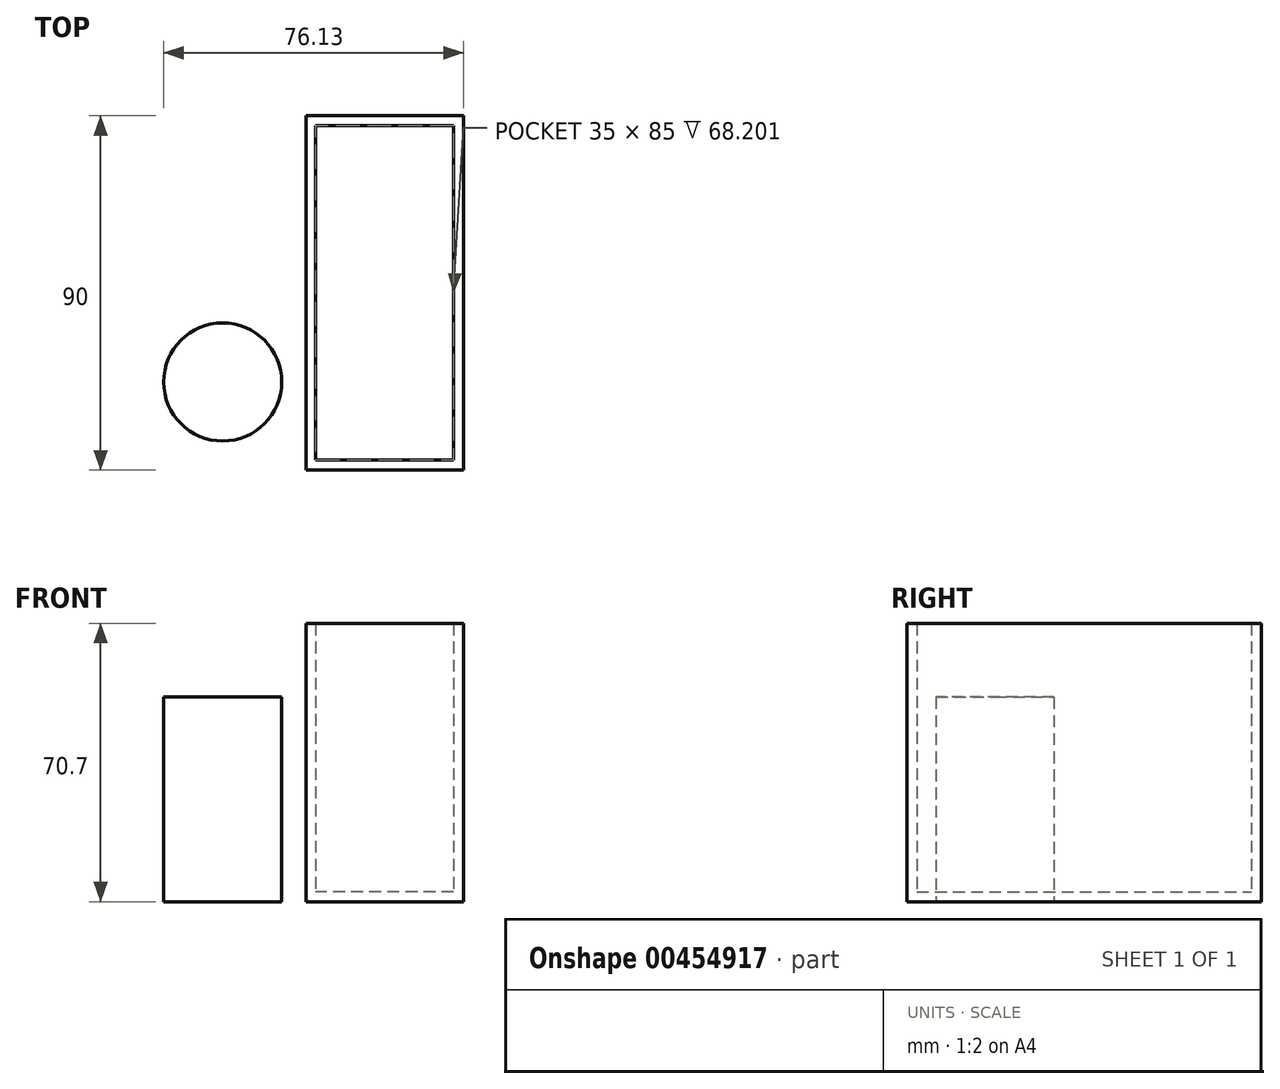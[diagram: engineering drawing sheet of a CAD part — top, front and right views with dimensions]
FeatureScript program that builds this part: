
annotation { "Feature Type Name" : "Feature", "Feature Type Description" : "" }
export const myFeature = defineFeature(function(context is Context, id is Id, definition is map)
    precondition{}
    {
        {
            var Q0;
            Q0=qCreatedBy(makeId("Top.planeOp"),FACE);
            var sketch = newSketch(context, id + "F0", { "sketchPlane" : qUnion([Q0])});
            skCircle(sketch, "E0", {"center": v(0, 0) * mm, "radius": 15 * mm});
            skSolve(sketch);
        }
        {
            var Q0;
            Q0 = qSketchRegion(id + "F0", true);
            var Q1;
            Q1=makeQuery(id+"F0.imprint","IMPRINT",FACE,{"disambiguationData":[TD([[makeQuery(id+"F0.imprint","IMPRINT",EDGE,{"derivedFrom":sQuery(id+"F0.wireOp",EDGE,"E0")}),1.0]])]});
            extrude(context, id + "F1", {"entities" : qUnion([Q0, Q1]), "depth" : 52 * mm});
        }
        {
            var Q0;
            Q0=qCreatedBy(makeId("Top.planeOp"),FACE);
            var sketch = newSketch(context, id + "F2", { "sketchPlane" : qUnion([Q0])});
            skLineSegment(sketch, "E1.bottom", {"start": v(61.13, -22.35) * mm, "end": v(21.13, -22.35) * mm});
            skLineSegment(sketch, "E1.top", {"start": v(61.13, 67.65) * mm, "end": v(21.13, 67.65) * mm});
            skLineSegment(sketch, "E1.left", {"start": v(61.13, -22.35) * mm, "end": v(61.13, 67.65) * mm});
            skLineSegment(sketch, "E1.right", {"start": v(21.13, -22.35) * mm, "end": v(21.13, 67.65) * mm});
            skPoint(sketch, "E1.middle", {"position": v(41.13, 22.65) * mm});
            skSolve(sketch);
        }
        {
            var Q0;
            Q0=makeQuery(id+"F2.imprint","IMPRINT",FACE,{"disambiguationData":[TD([[makeQuery(id+"F2.imprint","IMPRINT",EDGE,{"derivedFrom":sQuery(id+"F2.wireOp",EDGE,"E1.bottom")}),-1.0]])]});
            extrude(context, id + "F3", {"entities" : qUnion([Q0]), "depth" : 70.7 * mm});
        }
        {
            var Q0;
            Q0=makeQuery(id+"F3.opExtrude","CAP_FACE",FACE,{"disambiguationData":[OSD([sQuery(id+"F2.wireOp",EDGE,"E1.bottom"),sQuery(id+"F2.wireOp",EDGE,"E1.top"),sQuery(id+"F2.wireOp",EDGE,"E1.left"),sQuery(id+"F2.wireOp",EDGE,"E1.right")])],"isStart":false});
            shell(context, id + "F4", {"entities" : qUnion([Q0]), "thickness" : 2.5 * mm});
        }
    });
